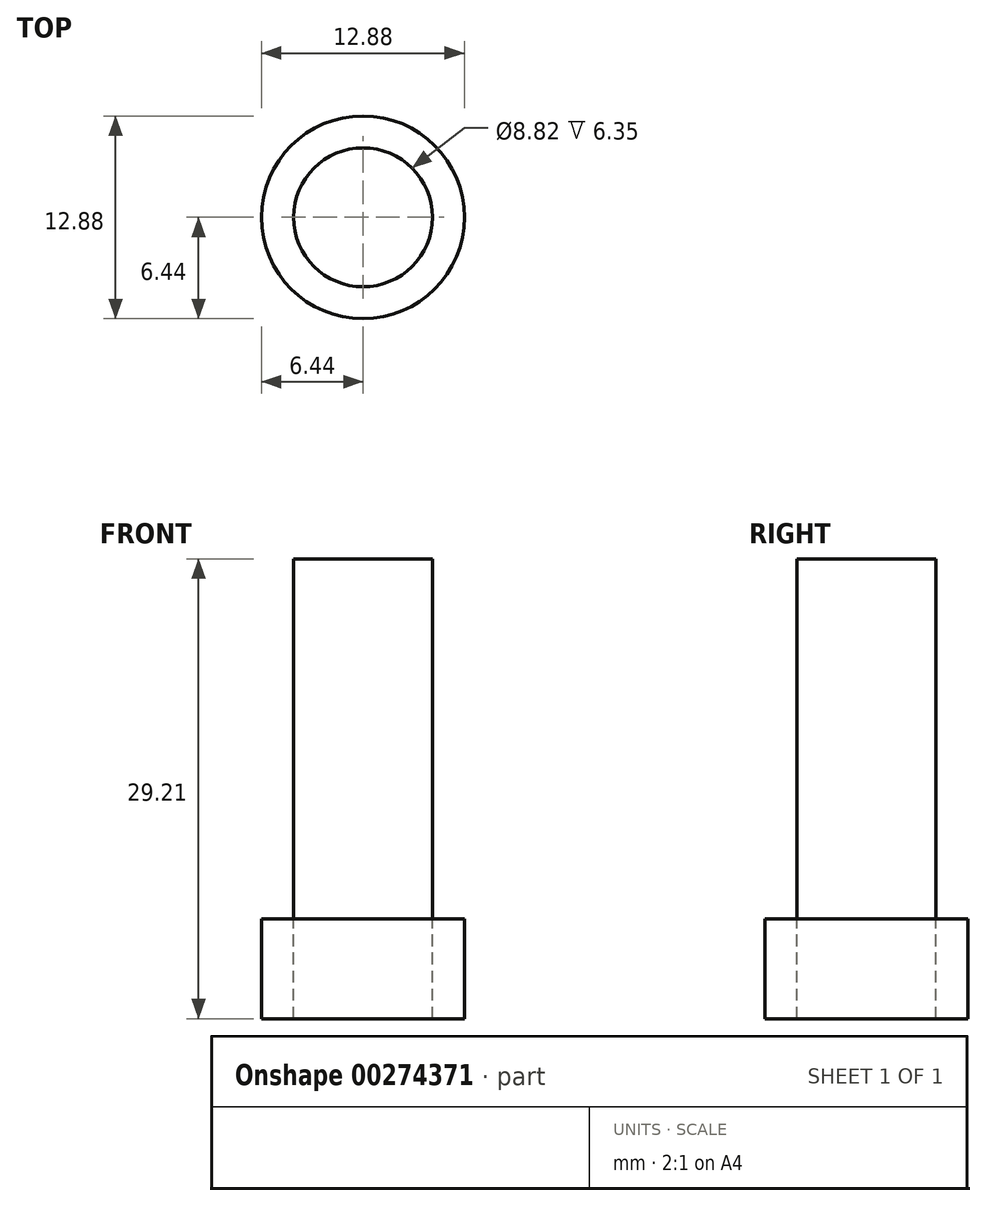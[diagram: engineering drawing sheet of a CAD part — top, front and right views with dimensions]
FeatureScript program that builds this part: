
annotation { "Feature Type Name" : "Feature", "Feature Type Description" : "" }
export const myFeature = defineFeature(function(context is Context, id is Id, definition is map)
    precondition{}
    {
        {
            var Q0;
            Q0=qCreatedBy(makeId("Top.planeOp"),FACE);
            var sketch = newSketch(context, id + "F0", { "sketchPlane" : qUnion([Q0])});
            skCircle(sketch, "E0", {"center": v(0, 0) * mm, "radius": 4.41 * mm});
            skCircle(sketch, "E1", {"center": v(0, 0) * mm, "radius": 6.44 * mm});
            skSolve(sketch);
        }
        {
            var Q0;
            Q0=makeQuery(id+"F0.imprint","IMPRINT",FACE,{"disambiguationData":[TD([[makeQuery(id+"F0.imprint","IMPRINT",EDGE,{"derivedFrom":sQuery(id+"F0.wireOp",EDGE,"E0")}),1.0]])]});
            extrude(context, id + "F1", {"entities" : qUnion([Q0]), "depth" : 22.86 * mm});
        }
        {
            var Q0;
            Q0=makeQuery(id+"F0.imprint","IMPRINT",FACE,{"disambiguationData":[TD([[makeQuery(id+"F0.imprint","IMPRINT",EDGE,{"derivedFrom":sQuery(id+"F0.wireOp",EDGE,"E0")}),-1.0]])]});
            extrude(context, id + "F2", {"entities" : qUnion([Q0]), "oppositeDirection" : true, "depth" : 6.35 * mm});
        }
    });
